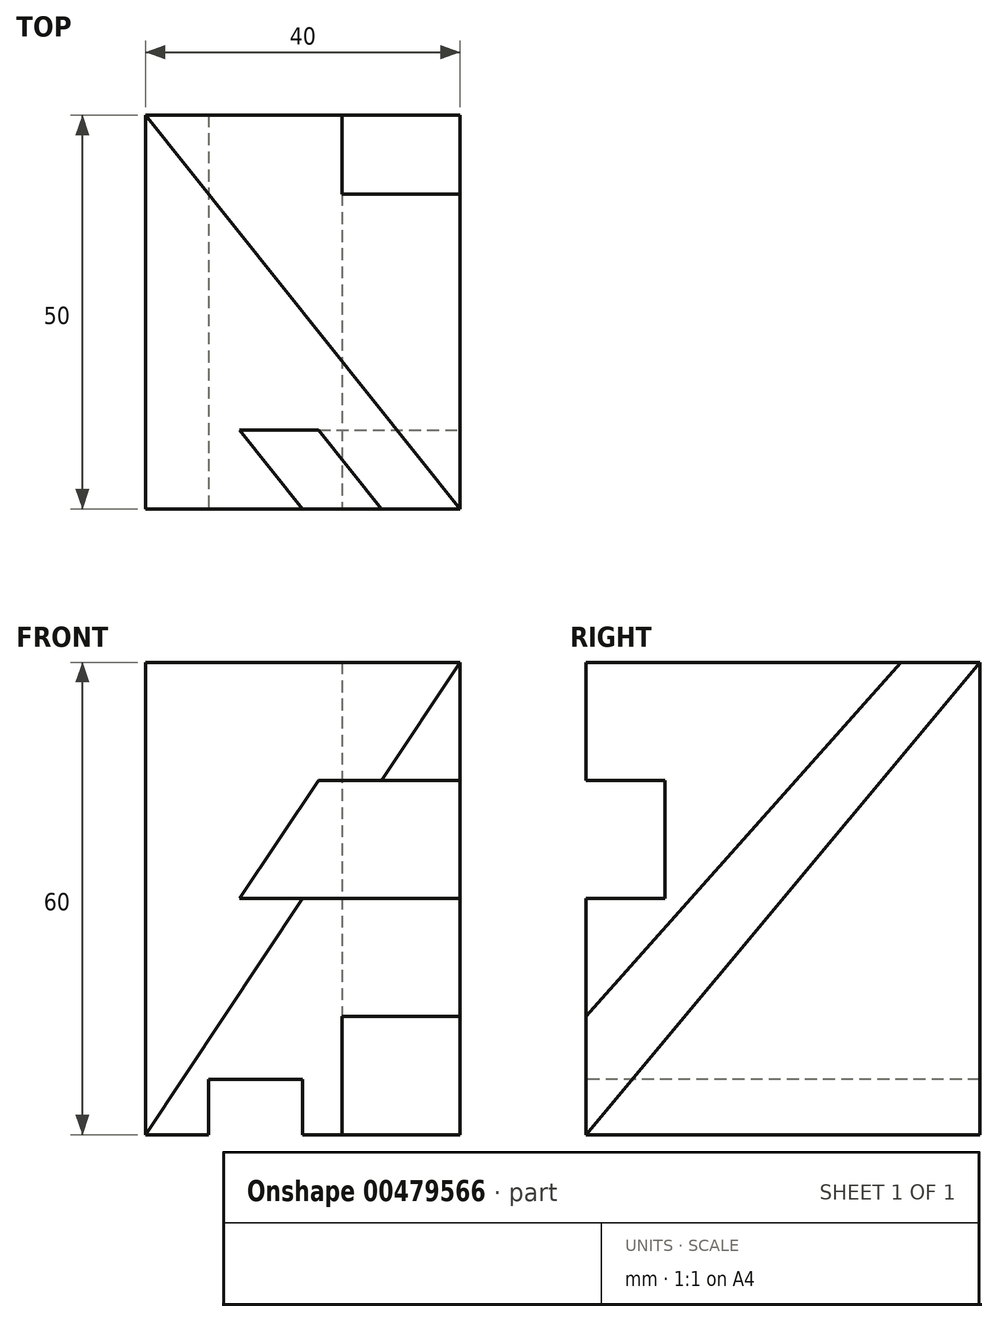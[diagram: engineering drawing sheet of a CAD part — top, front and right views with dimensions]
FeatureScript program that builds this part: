
annotation { "Feature Type Name" : "Feature", "Feature Type Description" : "" }
export const myFeature = defineFeature(function(context is Context, id is Id, definition is map)
    precondition{}
    {
        {
            var Q0;
            Q0=qCreatedBy(makeId("Front.planeOp"),FACE);
            var sketch = newSketch(context, id + "F0", { "sketchPlane" : qUnion([Q0])});
            skLineSegment(sketch, "E0.bottom", {"start": v(0, 0) * mm, "end": v(40, 0) * mm});
            skLineSegment(sketch, "E0.top", {"start": v(0, 60) * mm, "end": v(40, 60) * mm});
            skLineSegment(sketch, "E0.left", {"start": v(0, 0) * mm, "end": v(0, 60) * mm});
            skLineSegment(sketch, "E0.right", {"start": v(40, 0) * mm, "end": v(40, 60) * mm});
            skSolve(sketch);
        }
        {
            var Q0;
            Q0 = qSketchRegion(id + "F0", true);
            extrude(context, id + "F1", {"entities" : qUnion([Q0]), "depth" : 50 * mm});
        }
        {
            var Q0;
            Q0=makeQuery(id+"F1.opExtrude","SWEPT_FACE",FACE,{"disambiguationData":[OSD([sQuery(id+"F0.wireOp",EDGE,"E0.top")])]});
            var sketch = newSketch(context, id + "F2", { "sketchPlane" : qUnion([Q0])});
            skLineSegment(sketch, "E1", {"start": v(0, 0) * mm, "end": v(40, -50) * mm});
            skLineSegment(sketch, "E2", {"start": v(40, -50) * mm, "end": v(0, -50) * mm});
            skSolve(sketch);
        }
        {
            var Q1;
            Q1=makeQuery(id+"F2.imprint","IMPRINT",FACE,{"disambiguationData":[TD([[makeQuery(id+"F2.imprint","IMPRINT",EDGE,{"derivedFrom":sQuery(id+"F2.wireOp",EDGE,"E1")}),-1.0]])]});
            var Q2;
            Q2=makeQuery(id+"F1.opExtrude","CAP_VERTEX",VERTEX,{"disambiguationData":[OSD([sQuery(id+"F0.wireOp",EDGE,"E0.bottom"),sQuery(id+"F0.wireOp",EDGE,"E0.left")])],"isStart":false});
            loft(context, id + "F3", {"operationType" : NewBodyOperationType.REMOVE, "sheetProfilesArray" : [{ "sheetProfileEntities" : qUnion([Q1]) }, { "sheetProfileEntities" : qUnion([Q2]) }]});
        }
        {
            var Q0;
            Q0=makeQuery(id+"F1.opExtrude","CAP_FACE",FACE,{"disambiguationData":[OSD([sQuery(id+"F0.wireOp",EDGE,"E0.bottom"),sQuery(id+"F0.wireOp",EDGE,"E0.top"),sQuery(id+"F0.wireOp",EDGE,"E0.left"),sQuery(id+"F0.wireOp",EDGE,"E0.right")])],"isStart":false});
            var sketch = newSketch(context, id + "F4", { "sketchPlane" : qUnion([Q0])});
            skLineSegment(sketch, "E3.bottom", {"start": v(8, 0) * mm, "end": v(20, 0) * mm});
            skLineSegment(sketch, "E3.top", {"start": v(8, 7) * mm, "end": v(20, 7) * mm});
            skLineSegment(sketch, "E3.left", {"start": v(8, 0) * mm, "end": v(8, 7) * mm});
            skLineSegment(sketch, "E3.right", {"start": v(20, 0) * mm, "end": v(20, 7) * mm});
            skSolve(sketch);
        }
        {
            var Q0;
            Q0 = qSketchRegion(id + "F4", true);
            extrude(context, id + "F5", {"entities" : qUnion([Q0]), "operationType" : NewBodyOperationType.REMOVE, "endBound" : BoundingType.THROUGH_ALL, "oppositeDirection" : true, "depth" : 25 * mm});
        }
        {
            var Q0;
            Q0=makeQuery(id+"F1.opExtrude","CAP_FACE",FACE,{"disambiguationData":[OSD([sQuery(id+"F0.wireOp",EDGE,"E0.bottom"),sQuery(id+"F0.wireOp",EDGE,"E0.top"),sQuery(id+"F0.wireOp",EDGE,"E0.left"),sQuery(id+"F0.wireOp",EDGE,"E0.right")])],"isStart":false});
            var sketch = newSketch(context, id + "F6", { "sketchPlane" : qUnion([Q0])});
            skPoint(sketch, "E4.firstSnap0", {"position": v(20, 45) * mm});
            skLineSegment(sketch, "E4.bottom", {"start": v(0, 45) * mm, "end": v(40, 45) * mm});
            skLineSegment(sketch, "E4.top", {"start": v(0, 30) * mm, "end": v(40, 30) * mm});
            skLineSegment(sketch, "E4.left", {"start": v(0, 45) * mm, "end": v(0, 30) * mm});
            skLineSegment(sketch, "E4.right", {"start": v(40, 45) * mm, "end": v(40, 30) * mm});
            skSolve(sketch);
        }
        {
            var Q0;
            Q0 = qSketchRegion(id + "F6", true);
            extrude(context, id + "F7", {"entities" : qUnion([Q0]), "operationType" : NewBodyOperationType.REMOVE, "oppositeDirection" : true, "depth" : 10 * mm});
        }
        {
            var Q0;
            Q0=makeQuery(id+"F1.opExtrude","SWEPT_FACE",FACE,{"disambiguationData":[OSD([sQuery(id+"F0.wireOp",EDGE,"E0.right")])]});
            var sketch = newSketch(context, id + "F8", { "sketchPlane" : qUnion([Q0])});
            skLineSegment(sketch, "E5", {"start": v(0, 60) * mm, "end": v(-50, 0) * mm});
            skLineSegment(sketch, "E6", {"start": v(-50, 0) * mm, "end": v(-50, 15) * mm});
            skLineSegment(sketch, "E7", {"start": v(-50, 15) * mm, "end": v(-10, 60) * mm});
            skLineSegment(sketch, "E8", {"start": v(-10, 60) * mm, "end": v(0, 60) * mm});
            skSolve(sketch);
        }
        {
            var Q0;
            Q0 = qSketchRegion(id + "F8", true);
            extrude(context, id + "F9", {"entities" : qUnion([Q0]), "operationType" : NewBodyOperationType.REMOVE, "oppositeDirection" : true, "depth" : 15 * mm});
        }
    });
